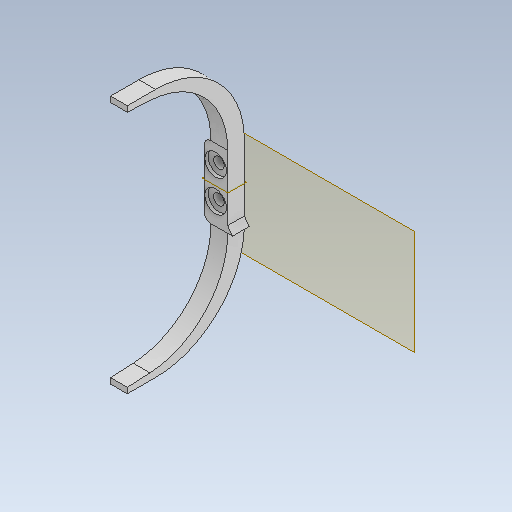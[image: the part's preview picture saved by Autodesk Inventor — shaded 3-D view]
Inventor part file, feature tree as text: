
AUTODESK INVENTOR PART (.ipt)
format: ipt  version: 2020 (Build 240168000, 168)  size: 161,280 bytes
history: native  units: mm
features: sketch x3, other x3, plane x2, extrude x2, hole x1, mirror x1, reference x1
ambient origin geometry x8: Origin, YZ Plane, XZ Plane, XY Plane, X Axis, Y Axis, Z Axis, Center Point
bodies: Solid1 (feature_tree)
feature tree (13):
  plane  "Work Plane1"
  extrude  "Extrusion1"  Depth=1.0mm
  plane  "Work Plane2"
  extrude  "Extrusion2"  Depth=35.0mm
  hole  "Hole1"  [1 undecoded]
  mirror  "Mirror1"
  sketch  "Sketch1"  dims[d0=5.0mm d1=0.0mm]
  reference  "Reference1"
  sketch  "Sketch2"  dims[d2=3.2mm d3=6.0mm d4=6.5mm d5=1.0mm d6=90.0deg d7=8.0mm d8=20.594885mm d9=3.0mm]
  sketch  "Sketch3"  dims[d10=5.0mm d11=0.0mm d12=35.0mm]
  parser-record x1  (decoder bookkeeping rows leaked as tree rows — omitted from the tree; the rows remain in map.json)
  other  "motorized.iam"
  other  "bracket:1"
note: 1 required parameter value undecoded (feature->parameter linkage not recoverable at this tier; creation-order binding heuristic only, values carry confidence <= 0.55)
note: 1 file-system path scrubbed to <path> (originals preserved in map.json)
